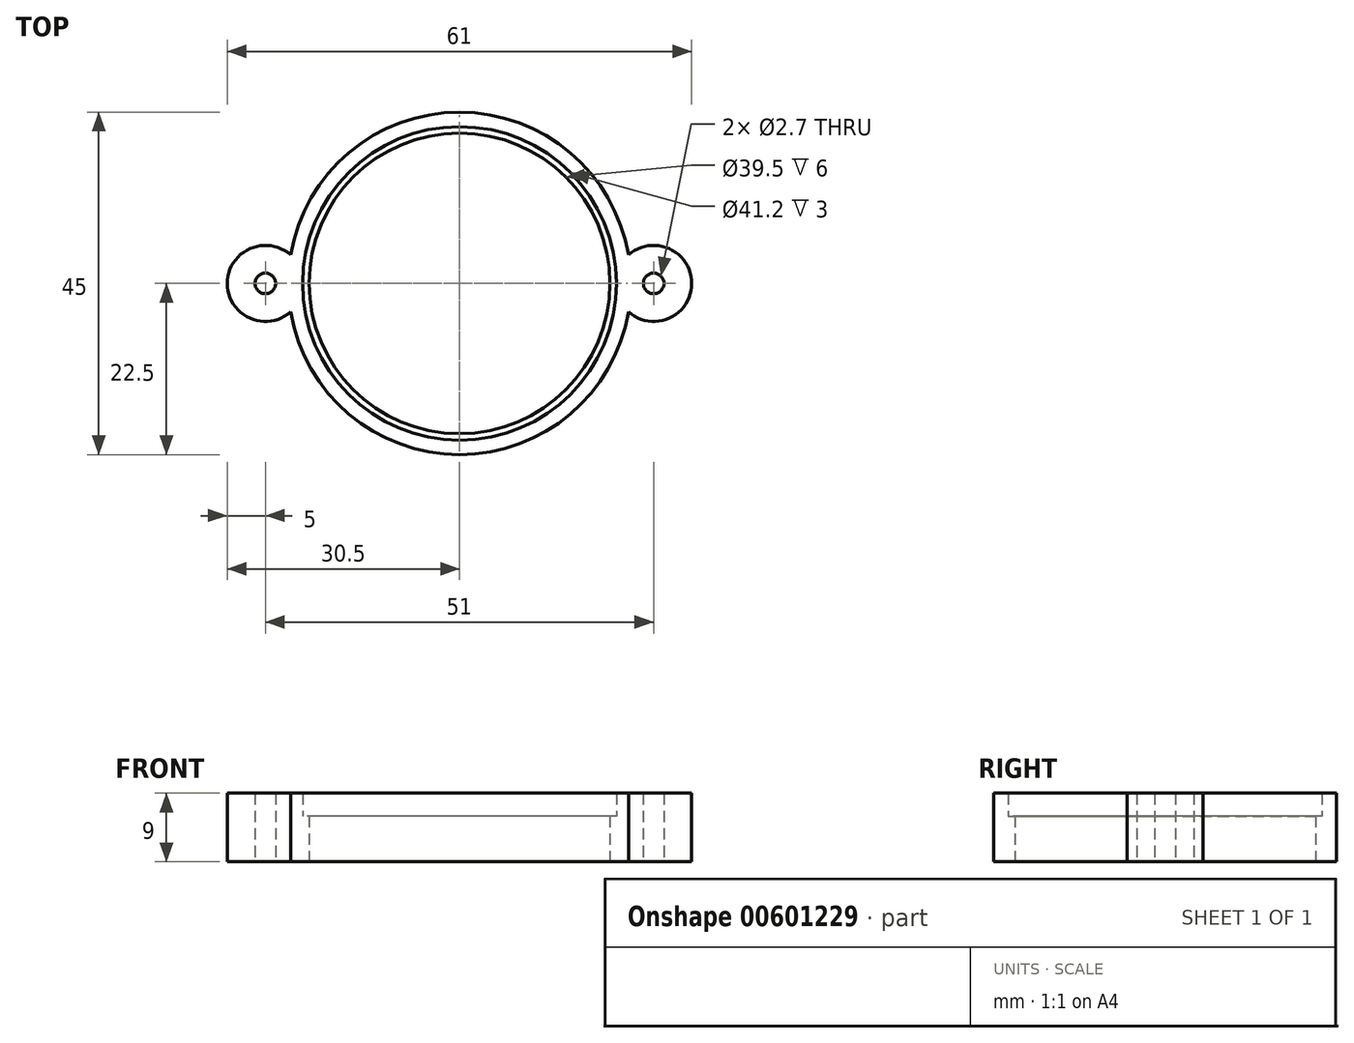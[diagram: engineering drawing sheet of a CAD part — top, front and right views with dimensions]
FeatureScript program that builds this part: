
annotation { "Feature Type Name" : "Feature", "Feature Type Description" : "" }
export const myFeature = defineFeature(function(context is Context, id is Id, definition is map)
    precondition{}
    {
        {
            var Q0;
            Q0=qCreatedBy(makeId("Top.planeOp"),FACE);
            var sketch = newSketch(context, id + "F0", { "sketchPlane" : qUnion([Q0])});
            skCircle(sketch, "E0", {"center": v(0, 0) * mm, "radius": 19.75 * mm});
            skCircle(sketch, "E1", {"center": v(0, 0) * mm, "radius": 22.5 * mm});
            skCircle(sketch, "E2", {"center": v(-25.5, 0) * mm, "radius": 5 * mm});
            skCircle(sketch, "E3", {"center": v(25.5, 0) * mm, "radius": 5 * mm});
            skCircle(sketch, "E4", {"center": v(-25.5, 0) * mm, "radius": 1.35 * mm});
            skCircle(sketch, "E5", {"center": v(25.5, 0) * mm, "radius": 1.35 * mm});
            skSolve(sketch);
        }
        {
            var Q0;
            Q0=makeQuery(id+"F0.imprint","IMPRINT",FACE,{"disambiguationData":[TD([[makeQuery(id+"F0.imprint","IMPRINT",EDGE,{"derivedFrom":sQuery(id+"F0.wireOp",EDGE,"E4")}),-1.0]])]});
            var Q1;
            Q1=makeQuery(id+"F0.imprint","IMPRINT",FACE,{"disambiguationData":[TD([[makeQuery(id+"F0.imprint","IMPRINT",EDGE,{"derivedFrom":sQuery(id+"F0.wireOp",EDGE,"E5")}),-1.0]])]});
            extrude(context, id + "F1", {"entities" : qUnion([Q0, Q1]), "depth" : 9 * mm, "offsetDistance" : 25 * mm});
        }
        {
            var Q0;
            Q0=makeQuery(id+"F0.imprint","IMPRINT",FACE,{"disambiguationData":[TD([[makeQuery(id+"F0.imprint","IMPRINT",EDGE,{"derivedFrom":sQuery(id+"F0.wireOp",EDGE,"E0")}),-1.0]])]});
            var Q1;
            {var subQ0=sQuery(id+"F0.wireOp",EDGE,"E3");var subQ1=sQuery(id+"F0.wireOp",EDGE,"E1");var subQ2=makeQuery(id+"F0.imprint","INTERSECT",VERTEX,{"disambiguationData":[OD(0.0)],"derivedFrom":[subQ1,subQ0]});Q1=makeQuery(id+"F0.imprint","IMPRINT",FACE,{"disambiguationData":[TD([[makeQuery(id+"F0.imprint","IMPRINT",EDGE,{"disambiguationData":[TD([[subQ2,1.0]])],"derivedFrom":subQ1}),1.0]])]});}
            var Q2;
            {var subQ0=sQuery(id+"F0.wireOp",EDGE,"E2");var subQ1=sQuery(id+"F0.wireOp",EDGE,"E1");var subQ2=makeQuery(id+"F0.imprint","INTERSECT",VERTEX,{"disambiguationData":[OD(0.0)],"derivedFrom":[subQ1,subQ0]});Q2=makeQuery(id+"F0.imprint","IMPRINT",FACE,{"disambiguationData":[TD([[makeQuery(id+"F0.imprint","IMPRINT",EDGE,{"disambiguationData":[TD([[subQ2,-1.0]])],"derivedFrom":subQ1}),1.0]])]});}
            extrude(context, id + "F2", {"entities" : qUnion([Q0, Q1, Q2]), "depth" : 6 * mm, "offsetDistance" : 25 * mm});
        }
        {
            var Q0;
            Q0=makeQuery(id+"F2.opExtrude","CAP_FACE",FACE,{"disambiguationData":[OSD([sQuery(id+"F0.wireOp",EDGE,"E0"),sQuery(id+"F0.wireOp",EDGE,"E1")])],"isStart":false});
            var sketch = newSketch(context, id + "F3", { "sketchPlane" : qUnion([Q0])});
            skCircle(sketch, "E6", {"center": v(0, 0) * mm, "radius": 20.6 * mm});
            skCircle(sketch, "E7", {"center": v(0, 0) * mm, "radius": 22.5 * mm});
            skSolve(sketch);
        }
        {
            var Q0;
            Q0=makeQuery(id+"F3.imprint","IMPRINT",FACE,{"disambiguationData":[TD([[makeQuery(id+"F3.imprint","IMPRINT",EDGE,{"derivedFrom":sQuery(id+"F3.wireOp",EDGE,"E6")}),-1.0]])]});
            extrude(context, id + "F4", {"entities" : qUnion([Q0]), "operationType" : NewBodyOperationType.ADD, "depth" : 3 * mm, "offsetDistance" : 25 * mm});
        }
    });
